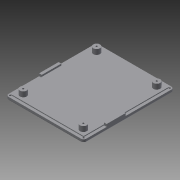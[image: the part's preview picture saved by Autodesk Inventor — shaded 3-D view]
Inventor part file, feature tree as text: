
AUTODESK INVENTOR PART (.ipt)
format: ipt  version: 2015 (Build 190159000, 159)  size: 211,968 bytes
history: native  units: in
note: dims shown in document units (in); Inventor stores cm internally (conversion verified against a paired STEP export)
features: extrude x5, hole x5, sketch x5, fillet x2
ambient origin geometry x8: Origin, YZ Plane, XZ Plane, XY Plane, X Axis, Y Axis, Z Axis, Center Point
bodies: Solid1 (feature_tree)
feature tree (17):
  extrude  "Extrusion1"  Depth=4.2126in
  extrude  "Extrusion2"  Depth=0.0787in
  extrude  "Extrusion3"  Depth=0.0984in
  hole  "Hole1"  [1 undecoded]
  hole  "Hole2"  [1 undecoded]
  hole  "Hole3"  [1 undecoded]
  hole  "Hole4"  [1 undecoded]
  hole  "Hole5"  [1 undecoded]
  fillet  "Fillet1"  Radius=3.4213in
  fillet  "Fillet2"  Radius=0.2697in
  extrude  "Extrusion5"  Depth=0.1181in
  extrude  "Extrusion6"  Depth=0.1181in
  sketch  "Sketch1"  dims[d0=3.622in d1=4.2126in]
  sketch  "Sketch2"  dims[d2=0.1378in d3=0.0in d4=0.0787in]
  sketch  "Sketch4"  dims[d5=0.0984in d6=0.0984in]
  sketch  "Sketch7"  dims[d7=2.1063in d8=1.811in]
  sketch  "Sketch8"  dims[d9=0.0787in d10=0.2362in d11=0.2362in d12=0.0787in d13=90.0deg d14=0.1969in d15=0.8108in d18=0.126in d19=0.126in d20=0.0394in d21=0.0in d24=2.8031in d25=3.4213in d26=0.2697in d27=0.2835in d28=0.315in d29=0.315in d30=0.315in d31=0.315in d32=0.2362in d33=0.0in d103=0.3937in d104=0.3937in d36=0.0787in d37=0.2362in d38=0.2362in d39=0.0787in d40=90.0deg d41=0.3543in d42=0.8108in d105=0.3937in d106=0.3937in d45=0.0787in d46=0.2362in d47=0.2362in d48=0.0787in d49=90.0deg d50=0.3543in d51=0.8108in d107=0.3937in d108=0.3937in d54=0.0787in d55=0.2362in d56=0.2362in d57=0.0787in d58=90.0deg d59=0.3543in d60=0.8108in d109=0.3937in d110=0.3937in d63=0.0787in d64=0.2362in d65=0.2362in d66=0.0787in d67=90.0deg d68=0.3543in d69=0.8108in d70=0.1181in d71=0.0394in d81=0.126in d82=0.126in d91=0.9055in d92=0.126in d93=1.5453in d94=0.1181in d95=0.0in d96=0.0in d97=0.8858in d98=0.0in d99=0.126in d100=1.0728in d101=0.1181in d102=0.0in]
note: 5 required parameter values undecoded (feature->parameter linkage not recoverable at this tier; creation-order binding heuristic only, values carry confidence <= 0.55)
